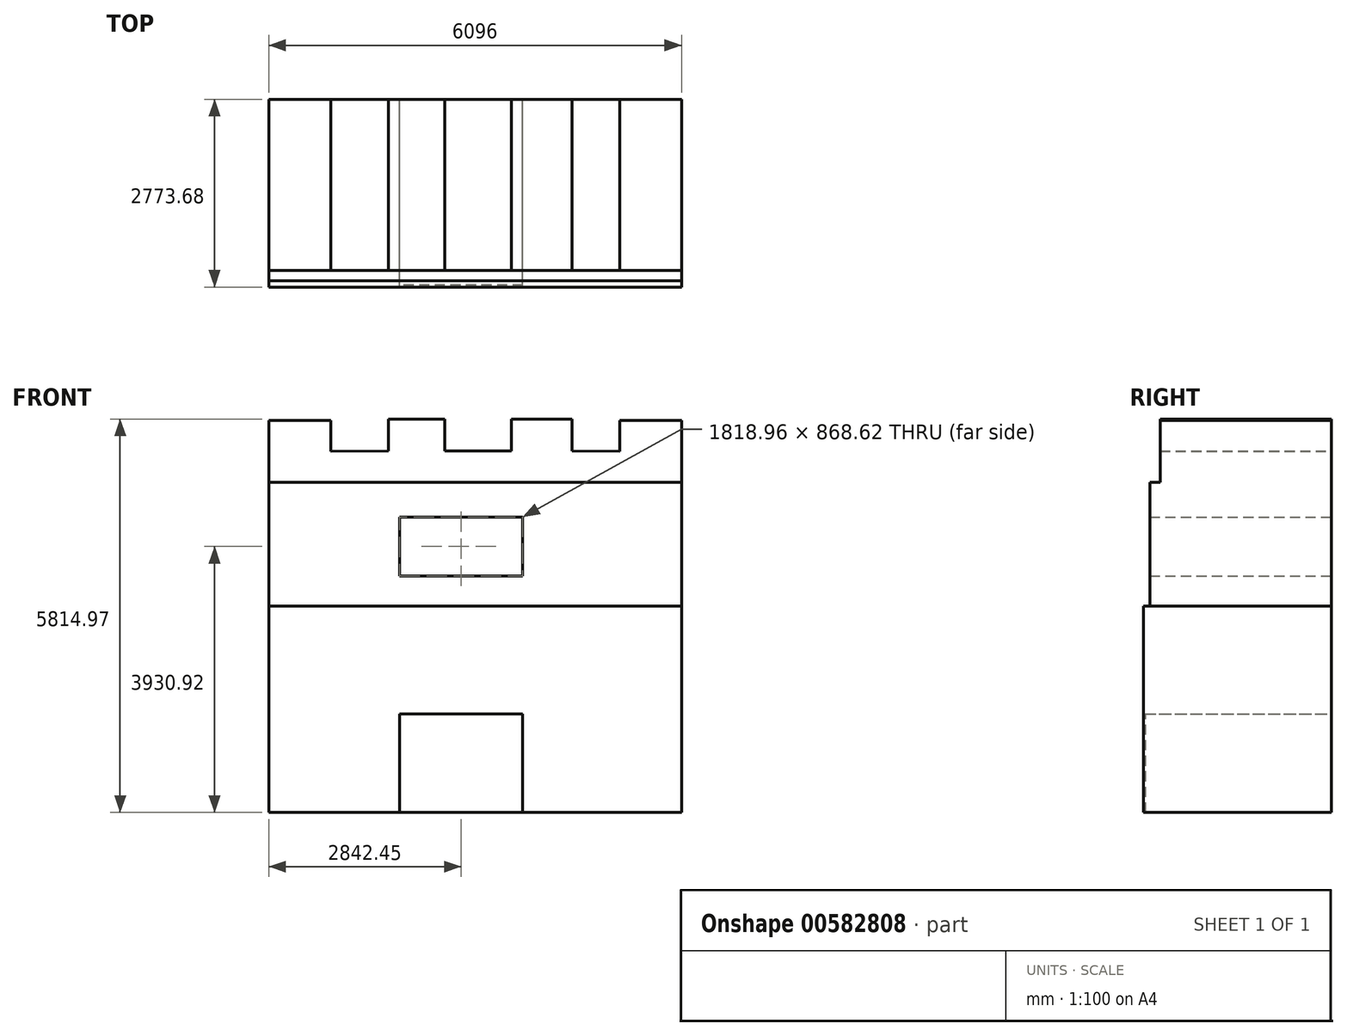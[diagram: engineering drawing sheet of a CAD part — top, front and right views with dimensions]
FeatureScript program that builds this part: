
annotation { "Feature Type Name" : "Feature", "Feature Type Description" : "" }
export const myFeature = defineFeature(function(context is Context, id is Id, definition is map)
    precondition{}
    {
        {
            var Q0;
            Q0=qCreatedBy(makeId("Front.planeOp"),FACE);
            var sketch = newSketch(context, id + "F0", { "sketchPlane" : qUnion([Q0])});
            skLineSegment(sketch, "E0", {"start": v(0, 0) * mm, "end": v(-3048, 0) * mm});
            skLineSegment(sketch, "E1", {"start": v(0, 0) * mm, "end": v(3048, 0) * mm});
            skLineSegment(sketch, "E2", {"start": v(-3048, 0) * mm, "end": v(-3048, 3048) * mm});
            skLineSegment(sketch, "E3", {"start": v(3048, 0) * mm, "end": v(3048, 3048) * mm});
            skLineSegment(sketch, "E4", {"start": v(3048, 3048) * mm, "end": v(-3048, 3048) * mm});
            skLineSegment(sketch, "E5", {"start": v(-3048, 3048) * mm, "end": v(-3048, 4876.8) * mm});
            skLineSegment(sketch, "E6", {"start": v(3048, 3048) * mm, "end": v(3048, 4876.8) * mm});
            skLineSegment(sketch, "E7", {"start": v(3048, 4876.8) * mm, "end": v(-3048, 4876.8) * mm});
            skLineSegment(sketch, "E8", {"start": v(-3048, 4876.8) * mm, "end": v(-3048, 5791.2) * mm});
            skLineSegment(sketch, "E9", {"start": v(-3048, 5791.2) * mm, "end": v(-2133.6, 5791.2) * mm});
            skLineSegment(sketch, "E10", {"start": v(-2133.6, 5791.2) * mm, "end": v(-2133.6, 4876.8) * mm});
            skLineSegment(sketch, "E11", {"start": v(3048, 4876.8) * mm, "end": v(3048, 5791.2) * mm});
            skLineSegment(sketch, "E12", {"start": v(3048, 5791.2) * mm, "end": v(2133.6, 5791.2) * mm});
            skLineSegment(sketch, "E13", {"start": v(2133.6, 5791.2) * mm, "end": v(2133.6, 4876.8) * mm});
            skPoint(sketch, "E14.end.orphan", {"position": v(2133.6, 5334) * mm});
            skPoint(sketch, "E14.start.orphan", {"position": v(-2133.6, 5334) * mm});
            skLineSegment(sketch, "E15", {"start": v(-1279.6, 4876.8) * mm, "end": v(-1279.6, 5814.97) * mm});
            skLineSegment(sketch, "E16", {"start": v(-1279.6, 5814.97) * mm, "end": v(-447.8, 5814.97) * mm});
            skLineSegment(sketch, "E17", {"start": v(-447.8, 5814.97) * mm, "end": v(-447.8, 4876.8) * mm});
            skLineSegment(sketch, "E18", {"start": v(1428.4, 4876.8) * mm, "end": v(1428.4, 5814.97) * mm});
            skLineSegment(sketch, "E19", {"start": v(1428.4, 5814.97) * mm, "end": v(538.62, 5814.97) * mm});
            skLineSegment(sketch, "E20", {"start": v(538.62, 5814.97) * mm, "end": v(538.62, 4876.8) * mm});
            skLineSegment(sketch, "E21", {"start": v(538.62, 5345.89) * mm, "end": v(-447.8, 5345.89) * mm});
            skLineSegment(sketch, "E22", {"start": v(-1279.6, 5345.89) * mm, "end": v(-2133.6, 5334) * mm});
            skLineSegment(sketch, "E23", {"start": v(1428.4, 5345.89) * mm, "end": v(2133.6, 5334) * mm});
            skLineSegment(sketch, "E24", {"start": v(-1115.02, 4400.42) * mm, "end": v(-1115.02, 3496.61) * mm});
            skLineSegment(sketch, "E25", {"start": v(-1115.02, 3496.61) * mm, "end": v(703.93, 3496.61) * mm});
            skLineSegment(sketch, "E26", {"start": v(703.93, 3496.61) * mm, "end": v(703.93, 4365.23) * mm});
            skLineSegment(sketch, "E27", {"start": v(703.93, 4365.23) * mm, "end": v(-1115.02, 4365.23) * mm});
            skLineSegment(sketch, "E28", {"start": v(-1115.02, 0) * mm, "end": v(-1115.02, 1458.16) * mm});
            skLineSegment(sketch, "E29", {"start": v(703.93, 0) * mm, "end": v(703.93, 1458.16) * mm});
            skLineSegment(sketch, "E30", {"start": v(703.93, 1458.16) * mm, "end": v(-1115.02, 1458.16) * mm});
            skSolve(sketch);
        }
        {
            var Q0;
            Q0=makeQuery(id+"F0.imprint","IMPRINT",FACE,{"disambiguationData":[TD([[makeQuery(id+"F0.imprint","IMPRINT",EDGE,{"derivedFrom":sQuery(id+"F0.wireOp",EDGE,"E4")}),-1.0]])]});
            extrude(context, id + "F1", {"entities" : qUnion([Q0]), "depth" : 2682.24 * mm, "offsetDistance" : 30.48 * mm});
        }
        {
            var Q0;
            Q0=makeQuery(id+"F0.imprint","IMPRINT",FACE,{"disambiguationData":[TD([[makeQuery(id+"F0.imprint","IMPRINT",EDGE,{"derivedFrom":sQuery(id+"F0.wireOp",EDGE,"E0")}),-1.0]])]});
            extrude(context, id + "F2", {"entities" : qUnion([Q0]), "operationType" : NewBodyOperationType.ADD, "depth" : 2743.2 * mm, "offsetDistance" : 30.48 * mm});
        }
        {
            var Q0;
            {var subQ3=sQuery(id+"F0.wireOp",EDGE,"E8");Q0=makeQuery(id+"F0.imprint","IMPRINT",FACE,{"disambiguationData":[TD([[makeQuery(id+"F0.imprint","IMPRINT",EDGE,{"derivedFrom":subQ3}),-1.0]])]});}
            var Q1;
            {var subQ5=sQuery(id+"F0.wireOp",EDGE,"E22");Q1=makeQuery(id+"F0.imprint","IMPRINT",FACE,{"disambiguationData":[TD([[makeQuery(id+"F0.imprint","IMPRINT",EDGE,{"derivedFrom":subQ5}),1.0]])]});}
            var Q2;
            {var subQ0=sQuery(id+"F0.wireOp",EDGE,"E16");Q2=makeQuery(id+"F0.imprint","IMPRINT",FACE,{"disambiguationData":[TD([[makeQuery(id+"F0.imprint","IMPRINT",EDGE,{"derivedFrom":subQ0}),-1.0]])]});}
            var Q3;
            {var subQ5=sQuery(id+"F0.wireOp",EDGE,"E21");Q3=makeQuery(id+"F0.imprint","IMPRINT",FACE,{"disambiguationData":[TD([[makeQuery(id+"F0.imprint","IMPRINT",EDGE,{"derivedFrom":subQ5}),1.0]])]});}
            var Q4;
            {var subQ0=sQuery(id+"F0.wireOp",EDGE,"E19");Q4=makeQuery(id+"F0.imprint","IMPRINT",FACE,{"disambiguationData":[TD([[makeQuery(id+"F0.imprint","IMPRINT",EDGE,{"derivedFrom":subQ0}),1.0]])]});}
            var Q5;
            {var subQ5=sQuery(id+"F0.wireOp",EDGE,"E23");Q5=makeQuery(id+"F0.imprint","IMPRINT",FACE,{"disambiguationData":[TD([[makeQuery(id+"F0.imprint","IMPRINT",EDGE,{"derivedFrom":subQ5}),-1.0]])]});}
            var Q6;
            {var subQ3=sQuery(id+"F0.wireOp",EDGE,"E11");Q6=makeQuery(id+"F0.imprint","IMPRINT",FACE,{"disambiguationData":[TD([[makeQuery(id+"F0.imprint","IMPRINT",EDGE,{"derivedFrom":subQ3}),1.0]])]});}
            extrude(context, id + "F3", {"entities" : qUnion([Q0, Q1, Q2, Q3, Q4, Q5, Q6]), "operationType" : NewBodyOperationType.ADD, "depth" : 2529.84 * mm, "offsetDistance" : 30.48 * mm});
        }
        {
            var Q0;
            {var subQ1=sQuery(id+"F0.wireOp",EDGE,"E2");Q0=makeQuery(id+"F0.imprint","IMPRINT",FACE,{"disambiguationData":[TD([[makeQuery(id+"F0.imprint","IMPRINT",EDGE,{"derivedFrom":subQ1}),-1.0]])]});}
            extrude(context, id + "F4", {"entities" : qUnion([Q0]), "depth" : 2773.68 * mm, "offsetDistance" : 30.48 * mm});
        }
    });
